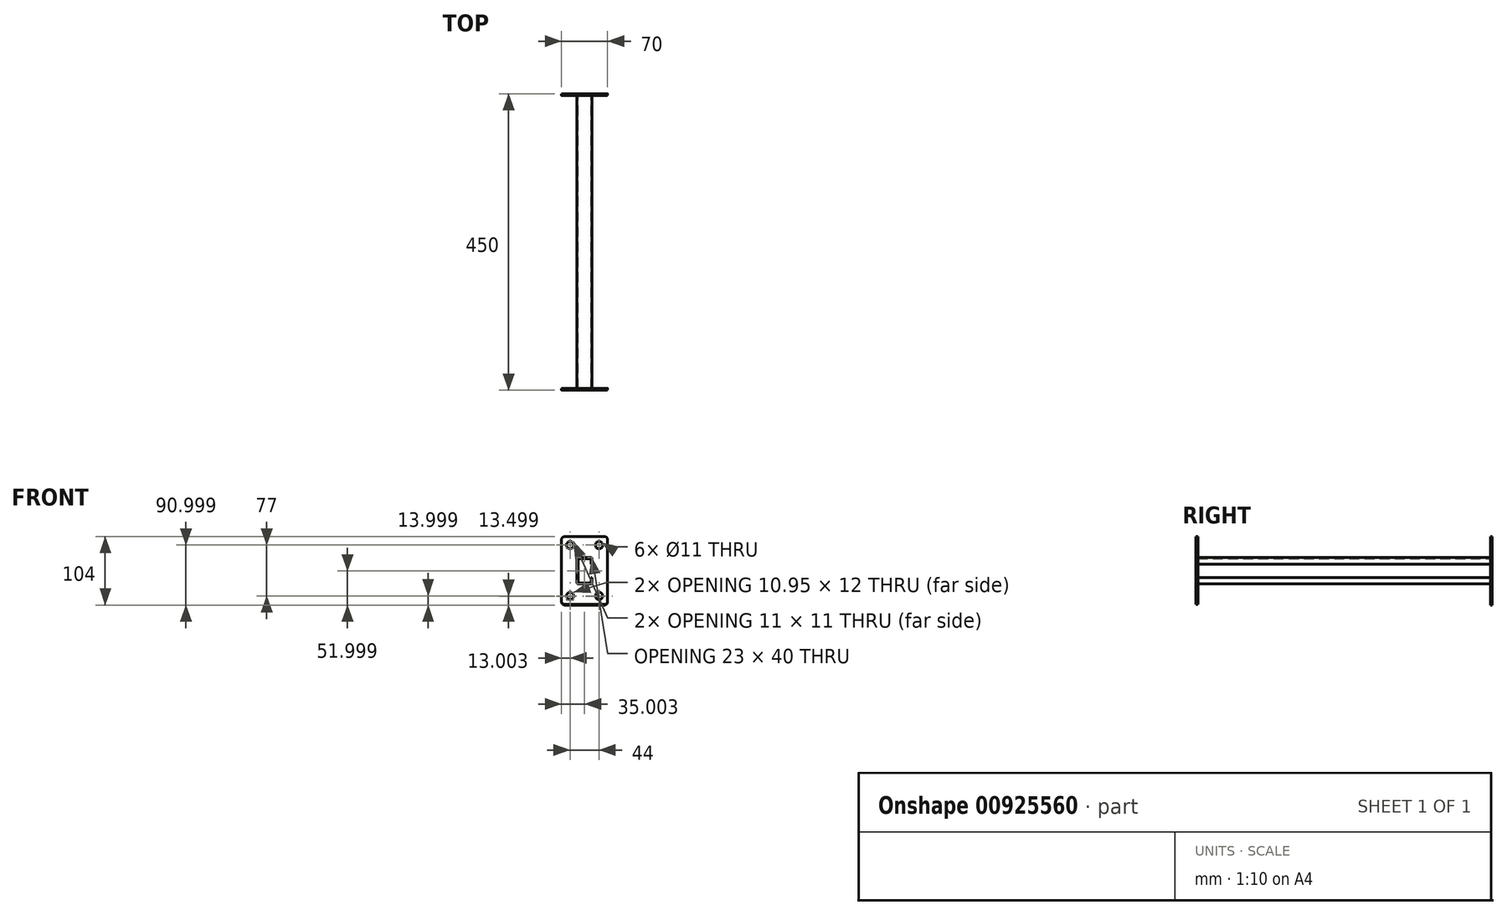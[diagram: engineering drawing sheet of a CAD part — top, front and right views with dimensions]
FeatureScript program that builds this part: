
annotation { "Feature Type Name" : "Feature", "Feature Type Description" : "" }
export const myFeature = defineFeature(function(context is Context, id is Id, definition is map)
    precondition{}
    {
        {
            var Q0;
            Q0=qCreatedBy(makeId("Front.planeOp"),FACE);
            var sketch = newSketch(context, id + "F0", { "sketchPlane" : qUnion([Q0])});
            skLineSegment(sketch, "E0.bottom", {"start": v(-106.84, 92.88) * mm, "end": v(-36.84, 92.88) * mm});
            skLineSegment(sketch, "E0.top", {"start": v(-106.84, -11.12) * mm, "end": v(-36.84, -11.12) * mm});
            skLineSegment(sketch, "E0.left", {"start": v(-106.84, 92.88) * mm, "end": v(-106.84, -11.12) * mm});
            skLineSegment(sketch, "E0.right", {"start": v(-36.84, 92.88) * mm, "end": v(-36.84, -11.12) * mm});
            skSolve(sketch);
        }
        {
            var Q0;
            Q0=makeQuery(id+"F0.imprint","IMPRINT",FACE,{"disambiguationData":[TD([[makeQuery(id+"F0.imprint","IMPRINT",EDGE,{"derivedFrom":sQuery(id+"F0.wireOp",EDGE,"E0.bottom")}),-1.0]])]});
            extrude(context, id + "F1", {"entities" : qUnion([Q0]), "depth" : 3 * mm, "offsetDistance" : 25 * mm});
        }
        {
            var Q0;
            Q0=makeQuery(id+"F1.opExtrude","SWEPT_EDGE",EDGE,{"disambiguationData":[OSD([sQuery(id+"F0.wireOp",EDGE,"E0.bottom"),sQuery(id+"F0.wireOp",EDGE,"E0.right")])]});
            var Q1;
            Q1=makeQuery(id+"F1.opExtrude","SWEPT_EDGE",EDGE,{"disambiguationData":[OSD([sQuery(id+"F0.wireOp",EDGE,"E0.bottom"),sQuery(id+"F0.wireOp",EDGE,"E0.left")])]});
            var Q2;
            Q2=makeQuery(id+"F1.opExtrude","SWEPT_EDGE",EDGE,{"disambiguationData":[OSD([sQuery(id+"F0.wireOp",EDGE,"E0.top"),sQuery(id+"F0.wireOp",EDGE,"E0.left")])]});
            var Q3;
            Q3=makeQuery(id+"F1.opExtrude","SWEPT_EDGE",EDGE,{"disambiguationData":[OSD([sQuery(id+"F0.wireOp",EDGE,"E0.top"),sQuery(id+"F0.wireOp",EDGE,"E0.right")])]});
            fillet(context, id + "F2", {"entities" : qUnion([Q0, Q1, Q2, Q3]), "radius" : 5 * mm, "tangentPropagation" : true, "allowEdgeOverflow" : false});
        }
        {
            var Q0;
            Q0=makeQuery(id+"F1.opExtrude","CAP_FACE",FACE,{"disambiguationData":[OSD([sQuery(id+"F0.wireOp",EDGE,"E0.bottom"),sQuery(id+"F0.wireOp",EDGE,"E0.top"),sQuery(id+"F0.wireOp",EDGE,"E0.left"),sQuery(id+"F0.wireOp",EDGE,"E0.right")])],"isStart":false});
            var sketch = newSketch(context, id + "F3", { "sketchPlane" : qUnion([Q0])});
            skCircle(sketch, "E1", {"center": v(-49.84, 1.88) * mm, "radius": 5.5 * mm});
            skCircle(sketch, "E2", {"center": v(-93.84, 1.88) * mm, "radius": 5.5 * mm});
            skCircle(sketch, "E3", {"center": v(-93.84, 79.88) * mm, "radius": 5.5 * mm});
            skCircle(sketch, "E4", {"center": v(-49.84, 79.88) * mm, "radius": 5.5 * mm});
            skSolve(sketch);
        }
        {
            var Q0;
            Q0=sQuery(id+"F3.wireOp",VERTEX,"E1.center");
            var Q1;
            Q1=sQuery(id+"F3.wireOp",VERTEX,"E2.center");
            var Q2;
            Q2=sQuery(id+"F3.wireOp",VERTEX,"E3.center");
            var Q3;
            Q3=sQuery(id+"F3.wireOp",VERTEX,"E4.center");
            var Q4;
            Q4=makeQuery(id+"F1.opExtrude","SWEPT_BODY",BODY,{"disambiguationData":[OSD([sQuery(id+"F0.wireOp",EDGE,"E0.bottom"),sQuery(id+"F0.wireOp",EDGE,"E0.top"),sQuery(id+"F0.wireOp",EDGE,"E0.left"),sQuery(id+"F0.wireOp",EDGE,"E0.right")])]});
            hole(context, id + "F4", {"style" : HoleStyle.SIMPLE, "endStyle" : HoleEndStyle.THROUGH, "holeDiameter" : 11 * mm, "majorDiameter" : 5 * mm, "isTappedThrough" : true, "tappedDepth" : 12 * mm, "tapClearance" : 3, "locations" : qUnion([Q0, Q1, Q2, Q3]), "scope" : qUnion([Q4])});
        }
        {
            var Q0;
            Q0=makeQuery(id+"F1.opExtrude","CAP_FACE",FACE,{"disambiguationData":[OSD([sQuery(id+"F0.wireOp",EDGE,"E0.bottom"),sQuery(id+"F0.wireOp",EDGE,"E0.top"),sQuery(id+"F0.wireOp",EDGE,"E0.left"),sQuery(id+"F0.wireOp",EDGE,"E0.right")])],"isStart":false});
            var sketch = newSketch(context, id + "F5", { "sketchPlane" : qUnion([Q0])});
            skPoint(sketch, "E5.visualSharp", {"position": v(-91.84, 27.27) * mm});
            skPoint(sketch, "E6.visualSharp", {"position": v(-90.34, 28.77) * mm});
            skLineSegment(sketch, "E7", {"start": v(-62.34, 60.88) * mm, "end": v(-81.34, 60.88) * mm});
            skLineSegment(sketch, "E8", {"start": v(-83.34, 58.88) * mm, "end": v(-83.34, 22.88) * mm});
            skLineSegment(sketch, "E9", {"start": v(-81.34, 20.88) * mm, "end": v(-62.34, 20.88) * mm});
            skLineSegment(sketch, "E10", {"start": v(-60.34, 22.88) * mm, "end": v(-60.34, 30.88) * mm});
            skLineSegment(sketch, "E11", {"start": v(-60.34, 30.88) * mm, "end": v(-61.84, 30.88) * mm});
            skLineSegment(sketch, "E12", {"start": v(-61.84, 30.88) * mm, "end": v(-61.84, 23.38) * mm});
            skLineSegment(sketch, "E13", {"start": v(-62.84, 22.38) * mm, "end": v(-80.84, 22.38) * mm});
            skLineSegment(sketch, "E14", {"start": v(-80.84, 59.38) * mm, "end": v(-62.84, 59.38) * mm});
            skLineSegment(sketch, "E15", {"start": v(-61.84, 58.38) * mm, "end": v(-61.84, 50.88) * mm});
            skLineSegment(sketch, "E16", {"start": v(-61.84, 50.88) * mm, "end": v(-60.34, 50.88) * mm});
            skLineSegment(sketch, "E17", {"start": v(-60.34, 58.88) * mm, "end": v(-60.34, 50.88) * mm});
            skLineSegment(sketch, "E18", {"start": v(-81.84, 58.38) * mm, "end": v(-81.84, 23.38) * mm});
            skPoint(sketch, "E19.visualSharp", {"position": v(-60.34, 60.88) * mm});
            skArc(sketch, "E19.filletArc", {"start": v(-60.34, 58.88) * mm, "mid": v(-60.92, 60.3) * mm, "end": v(-62.34, 60.88) * mm});
            skPoint(sketch, "E20.visualSharp", {"position": v(-60.34, 20.88) * mm});
            skArc(sketch, "E20.filletArc", {"start": v(-62.34, 20.88) * mm, "mid": v(-60.92, 21.46) * mm, "end": v(-60.34, 22.88) * mm});
            skPoint(sketch, "E21.visualSharp", {"position": v(-83.34, 20.88) * mm});
            skArc(sketch, "E21.filletArc", {"start": v(-83.34, 22.88) * mm, "mid": v(-82.75, 21.46) * mm, "end": v(-81.34, 20.88) * mm});
            skPoint(sketch, "E22.visualSharp", {"position": v(-83.34, 60.88) * mm});
            skArc(sketch, "E22.filletArc", {"start": v(-81.34, 60.88) * mm, "mid": v(-82.75, 60.3) * mm, "end": v(-83.34, 58.88) * mm});
            skPoint(sketch, "E23.visualSharp", {"position": v(-81.84, 59.38) * mm});
            skArc(sketch, "E23.filletArc", {"start": v(-80.84, 59.38) * mm, "mid": v(-81.54, 59.09) * mm, "end": v(-81.84, 58.38) * mm});
            skPoint(sketch, "E24.visualSharp", {"position": v(-61.84, 59.38) * mm});
            skArc(sketch, "E24.filletArc", {"start": v(-61.84, 58.38) * mm, "mid": v(-62.13, 59.09) * mm, "end": v(-62.84, 59.38) * mm});
            skPoint(sketch, "E25.visualSharp", {"position": v(-61.84, 22.38) * mm});
            skArc(sketch, "E25.filletArc", {"start": v(-62.84, 22.38) * mm, "mid": v(-62.13, 22.67) * mm, "end": v(-61.84, 23.38) * mm});
            skPoint(sketch, "E26.visualSharp", {"position": v(-81.84, 22.38) * mm});
            skArc(sketch, "E26.filletArc", {"start": v(-81.84, 23.38) * mm, "mid": v(-81.54, 22.67) * mm, "end": v(-80.84, 22.38) * mm});
            skSolve(sketch);
        }
        {
            var Q0;
            Q0=makeQuery(id+"F5.imprint","IMPRINT",FACE,{"disambiguationData":[TD([[makeQuery(id+"F5.imprint","IMPRINT",EDGE,{"derivedFrom":sQuery(id+"F5.wireOp",EDGE,"E7")}),1.0]])]});
            extrude(context, id + "F6", {"entities" : qUnion([Q0]), "operationType" : NewBodyOperationType.ADD, "depth" : 444 * mm, "offsetDistance" : 25 * mm});
        }
        {
            var Q0;
            Q0=makeQuery(id+"F6.opExtrude","CAP_FACE",FACE,{"disambiguationData":[OSD([sQuery(id+"F5.wireOp",EDGE,"E7"),sQuery(id+"F5.wireOp",EDGE,"E8"),sQuery(id+"F5.wireOp",EDGE,"E9"),sQuery(id+"F5.wireOp",EDGE,"E10"),sQuery(id+"F5.wireOp",EDGE,"E11"),sQuery(id+"F5.wireOp",EDGE,"E12"),sQuery(id+"F5.wireOp",EDGE,"E13"),sQuery(id+"F5.wireOp",EDGE,"E14"),sQuery(id+"F5.wireOp",EDGE,"E15"),sQuery(id+"F5.wireOp",EDGE,"E16"),sQuery(id+"F5.wireOp",EDGE,"E17"),sQuery(id+"F5.wireOp",EDGE,"E18"),sQuery(id+"F5.wireOp",EDGE,"E19.filletArc"),sQuery(id+"F5.wireOp",EDGE,"E20.filletArc"),sQuery(id+"F5.wireOp",EDGE,"E21.filletArc"),sQuery(id+"F5.wireOp",EDGE,"E22.filletArc"),sQuery(id+"F5.wireOp",EDGE,"E23.filletArc"),sQuery(id+"F5.wireOp",EDGE,"E24.filletArc"),sQuery(id+"F5.wireOp",EDGE,"E25.filletArc"),sQuery(id+"F5.wireOp",EDGE,"E26.filletArc")])],"isStart":false});
            var sketch = newSketch(context, id + "F7", { "sketchPlane" : qUnion([Q0])});
            skLineSegment(sketch, "E27", {"start": v(-36.84, 92.88) * mm, "end": v(-36.84, -10.12) * mm});
            skLineSegment(sketch, "E28", {"start": v(-36.84, -10.12) * mm, "end": v(-106.84, -10.12) * mm});
            skLineSegment(sketch, "E29", {"start": v(-106.84, -10.12) * mm, "end": v(-106.84, 92.88) * mm});
            skLineSegment(sketch, "E30", {"start": v(-106.84, 92.88) * mm, "end": v(-36.84, 92.88) * mm});
            skSolve(sketch);
        }
        {
            var Q0;
            Q0=makeQuery(id+"F7.imprint","IMPRINT",FACE,{"disambiguationData":[TD([[makeQuery(id+"F7.imprint","IMPRINT",EDGE,{"derivedFrom":sQuery(id+"F7.wireOp",EDGE,"E27")}),-1.0]])]});
            extrude(context, id + "F8", {"entities" : qUnion([Q0]), "depth" : 3 * mm, "offsetDistance" : 25 * mm});
        }
        {
            var Q0;
            Q0=makeQuery(id+"F6.opExtrude","CAP_FACE",FACE,{"disambiguationData":[OSD([sQuery(id+"F5.wireOp",EDGE,"E7"),sQuery(id+"F5.wireOp",EDGE,"E8"),sQuery(id+"F5.wireOp",EDGE,"E9"),sQuery(id+"F5.wireOp",EDGE,"E10"),sQuery(id+"F5.wireOp",EDGE,"E11"),sQuery(id+"F5.wireOp",EDGE,"E12"),sQuery(id+"F5.wireOp",EDGE,"E13"),sQuery(id+"F5.wireOp",EDGE,"E14"),sQuery(id+"F5.wireOp",EDGE,"E15"),sQuery(id+"F5.wireOp",EDGE,"E16"),sQuery(id+"F5.wireOp",EDGE,"E17"),sQuery(id+"F5.wireOp",EDGE,"E18"),sQuery(id+"F5.wireOp",EDGE,"E19.filletArc"),sQuery(id+"F5.wireOp",EDGE,"E20.filletArc"),sQuery(id+"F5.wireOp",EDGE,"E21.filletArc"),sQuery(id+"F5.wireOp",EDGE,"E22.filletArc"),sQuery(id+"F5.wireOp",EDGE,"E23.filletArc"),sQuery(id+"F5.wireOp",EDGE,"E24.filletArc"),sQuery(id+"F5.wireOp",EDGE,"E25.filletArc"),sQuery(id+"F5.wireOp",EDGE,"E26.filletArc")])],"isStart":false});
            extrude(context, id + "F9", {"entities" : qUnion([Q0]), "depth" : 3 * mm, "offsetDistance" : 25 * mm});
        }
        {
            var Q0;
            Q0=makeQuery(id+"F8.opExtrude","SWEPT_EDGE",EDGE,{"disambiguationData":[OSD([sQuery(id+"F7.wireOp",EDGE,"E27"),sQuery(id+"F7.wireOp",EDGE,"E30")])]});
            var Q1;
            Q1=makeQuery(id+"F8.opExtrude","SWEPT_EDGE",EDGE,{"disambiguationData":[OSD([sQuery(id+"F7.wireOp",EDGE,"E29"),sQuery(id+"F7.wireOp",EDGE,"E30")])]});
            var Q2;
            Q2=makeQuery(id+"F8.opExtrude","SWEPT_EDGE",EDGE,{"disambiguationData":[OSD([sQuery(id+"F7.wireOp",EDGE,"E28"),sQuery(id+"F7.wireOp",EDGE,"E29")])]});
            var Q3;
            Q3=makeQuery(id+"F8.opExtrude","SWEPT_EDGE",EDGE,{"disambiguationData":[OSD([sQuery(id+"F7.wireOp",EDGE,"E27"),sQuery(id+"F7.wireOp",EDGE,"E28")])]});
            fillet(context, id + "F10", {"entities" : qUnion([Q0, Q1, Q2, Q3]), "radius" : 5 * mm, "tangentPropagation" : true, "allowEdgeOverflow" : false});
        }
        {
            var Q0;
            Q0=makeQuery(id+"F8.opExtrude","CAP_FACE",FACE,{"disambiguationData":[OSD([sQuery(id+"F5.wireOp",EDGE,"E7"),sQuery(id+"F5.wireOp",EDGE,"E8"),sQuery(id+"F5.wireOp",EDGE,"E9"),sQuery(id+"F5.wireOp",EDGE,"E10"),sQuery(id+"F5.wireOp",EDGE,"E11"),sQuery(id+"F5.wireOp",EDGE,"E12"),sQuery(id+"F5.wireOp",EDGE,"E13"),sQuery(id+"F5.wireOp",EDGE,"E14"),sQuery(id+"F5.wireOp",EDGE,"E15"),sQuery(id+"F5.wireOp",EDGE,"E16"),sQuery(id+"F5.wireOp",EDGE,"E17"),sQuery(id+"F5.wireOp",EDGE,"E18"),sQuery(id+"F5.wireOp",EDGE,"E19.filletArc"),sQuery(id+"F5.wireOp",EDGE,"E20.filletArc"),sQuery(id+"F5.wireOp",EDGE,"E21.filletArc"),sQuery(id+"F5.wireOp",EDGE,"E22.filletArc"),sQuery(id+"F5.wireOp",EDGE,"E23.filletArc"),sQuery(id+"F5.wireOp",EDGE,"E24.filletArc"),sQuery(id+"F5.wireOp",EDGE,"E25.filletArc"),sQuery(id+"F5.wireOp",EDGE,"E26.filletArc"),sQuery(id+"F7.wireOp",EDGE,"E27"),sQuery(id+"F7.wireOp",EDGE,"E28"),sQuery(id+"F7.wireOp",EDGE,"E29"),sQuery(id+"F7.wireOp",EDGE,"E30")])],"isStart":false});
            var sketch = newSketch(context, id + "F11", { "sketchPlane" : qUnion([Q0])});
            skCircle(sketch, "E31", {"center": v(-93.84, 2.88) * mm, "radius": 5.5 * mm});
            skCircle(sketch, "E32", {"center": v(-93.84, 79.88) * mm, "radius": 5.5 * mm});
            skCircle(sketch, "E33", {"center": v(-49.84, 79.88) * mm, "radius": 5.5 * mm});
            skCircle(sketch, "E34", {"center": v(-49.84, 2.88) * mm, "radius": 5.5 * mm});
            skSolve(sketch);
        }
        {
            var Q0;
            Q0=sQuery(id+"F11.wireOp",VERTEX,"E32.center");
            var Q1;
            Q1=sQuery(id+"F11.wireOp",VERTEX,"E33.center");
            var Q2;
            Q2=sQuery(id+"F11.wireOp",VERTEX,"E34.center");
            var Q3;
            Q3=sQuery(id+"F11.wireOp",VERTEX,"E31.center");
            var Q4;
            Q4=makeQuery(id+"F1.opExtrude","SWEPT_BODY",BODY,{"disambiguationData":[OSD([sQuery(id+"F0.wireOp",EDGE,"E0.bottom"),sQuery(id+"F0.wireOp",EDGE,"E0.top"),sQuery(id+"F0.wireOp",EDGE,"E0.left"),sQuery(id+"F0.wireOp",EDGE,"E0.right")])]});
            var Q5;
            Q5=makeQuery(id+"F8.opExtrude","SWEPT_BODY",BODY,{"disambiguationData":[OSD([sQuery(id+"F5.wireOp",EDGE,"E7"),sQuery(id+"F5.wireOp",EDGE,"E8"),sQuery(id+"F5.wireOp",EDGE,"E9"),sQuery(id+"F5.wireOp",EDGE,"E10"),sQuery(id+"F5.wireOp",EDGE,"E11"),sQuery(id+"F5.wireOp",EDGE,"E12"),sQuery(id+"F5.wireOp",EDGE,"E13"),sQuery(id+"F5.wireOp",EDGE,"E14"),sQuery(id+"F5.wireOp",EDGE,"E15"),sQuery(id+"F5.wireOp",EDGE,"E16"),sQuery(id+"F5.wireOp",EDGE,"E17"),sQuery(id+"F5.wireOp",EDGE,"E18"),sQuery(id+"F5.wireOp",EDGE,"E19.filletArc"),sQuery(id+"F5.wireOp",EDGE,"E20.filletArc"),sQuery(id+"F5.wireOp",EDGE,"E21.filletArc"),sQuery(id+"F5.wireOp",EDGE,"E22.filletArc"),sQuery(id+"F5.wireOp",EDGE,"E23.filletArc"),sQuery(id+"F5.wireOp",EDGE,"E24.filletArc"),sQuery(id+"F5.wireOp",EDGE,"E25.filletArc"),sQuery(id+"F5.wireOp",EDGE,"E26.filletArc"),sQuery(id+"F7.wireOp",EDGE,"E27"),sQuery(id+"F7.wireOp",EDGE,"E28"),sQuery(id+"F7.wireOp",EDGE,"E29"),sQuery(id+"F7.wireOp",EDGE,"E30")])]});
            hole(context, id + "F12", {"style" : HoleStyle.SIMPLE, "endStyle" : HoleEndStyle.THROUGH, "holeDiameter" : 11 * mm, "majorDiameter" : 5 * mm, "isTappedThrough" : true, "tappedDepth" : 12 * mm, "tapClearance" : 3, "locations" : qUnion([Q0, Q1, Q2, Q3]), "scope" : qUnion([Q4, Q5])});
        }
    });
